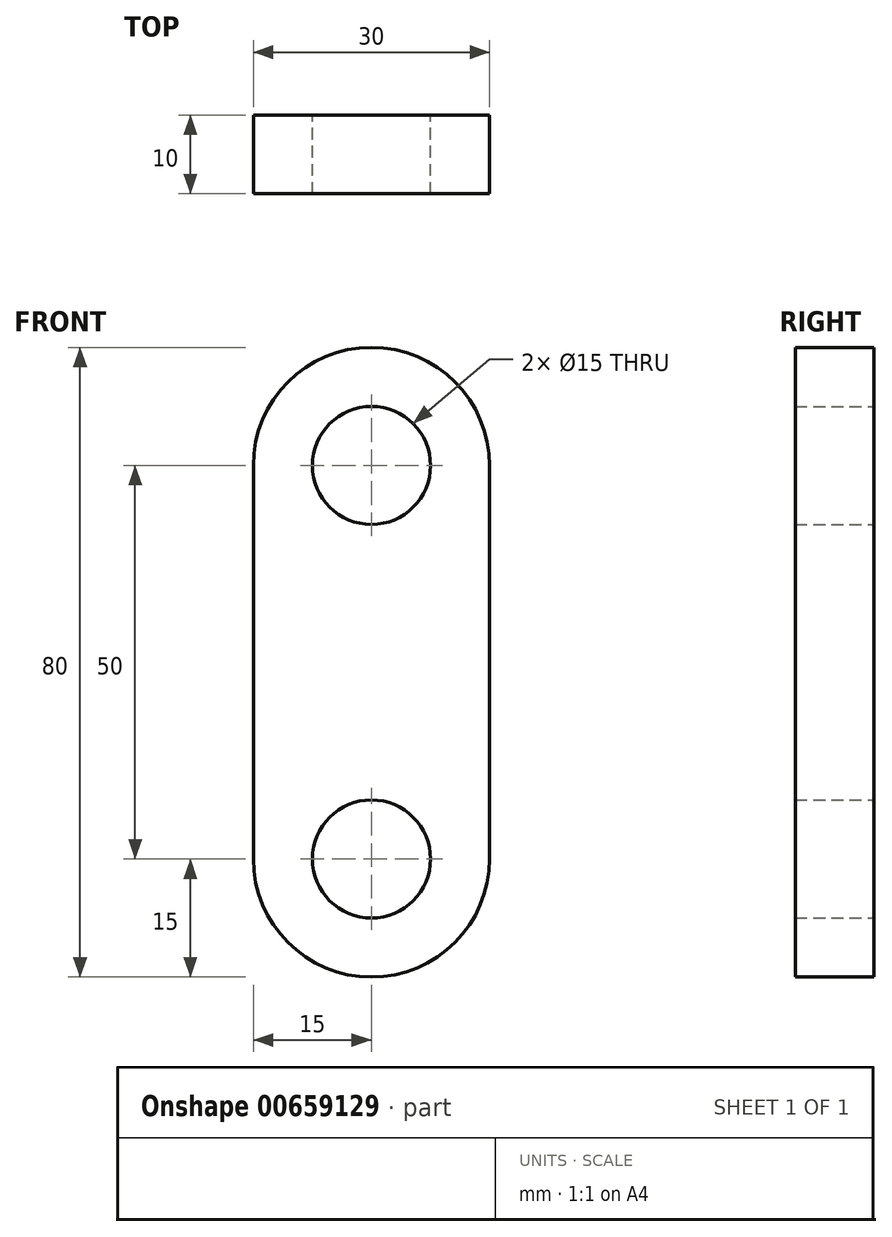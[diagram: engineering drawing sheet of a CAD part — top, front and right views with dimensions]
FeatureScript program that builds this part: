
annotation { "Feature Type Name" : "Feature", "Feature Type Description" : "" }
export const myFeature = defineFeature(function(context is Context, id is Id, definition is map)
    precondition{}
    {
        {
            var Q0;
            Q0=qCreatedBy(makeId("Front.planeOp"),FACE);
            var sketch = newSketch(context, id + "F0", { "sketchPlane" : qUnion([Q0])});
            skLineSegment(sketch, "E0", {"start": v(0, 40) * mm, "end": v(0, 0) * mm, "construction": true});
            skLineSegment(sketch, "E1", {"start": v(-15, 0) * mm, "end": v(15, 0) * mm, "construction": true});
            skCircle(sketch, "E2", {"center": v(0, 25) * mm, "radius": 7.5 * mm});
            skArc(sketch, "E3", {"start": v(15, 25) * mm, "mid": v(0, 40) * mm, "end": v(-15, 25) * mm});
            skLineSegment(sketch, "E4", {"start": v(-15, 25) * mm, "end": v(-15, 0) * mm});
            skLineSegment(sketch, "E5", {"start": v(15, 25) * mm, "end": v(15, 0) * mm});
            skArc(sketch, "E6.MirrorCS", {"start": v(15, -25) * mm, "mid": v(0, -40) * mm, "end": v(-15, -25) * mm});
            skCircle(sketch, "E7.MirrorC", {"center": v(0, -25) * mm, "radius": 7.5 * mm});
            skLineSegment(sketch, "E8.MirrorCS", {"start": v(15, -25) * mm, "end": v(15, 0) * mm});
            skLineSegment(sketch, "E9.MirrorCS", {"start": v(-15, -25) * mm, "end": v(-15, 0) * mm});
            skSolve(sketch);
        }
        {
            var Q0;
            Q0=qSketchRegion(id+"F0",true);
            extrude(context, id + "F1", {"entities" : qUnion([Q0]), "depth" : 10 * mm, "offsetDistance" : 25 * mm});
        }
    });
